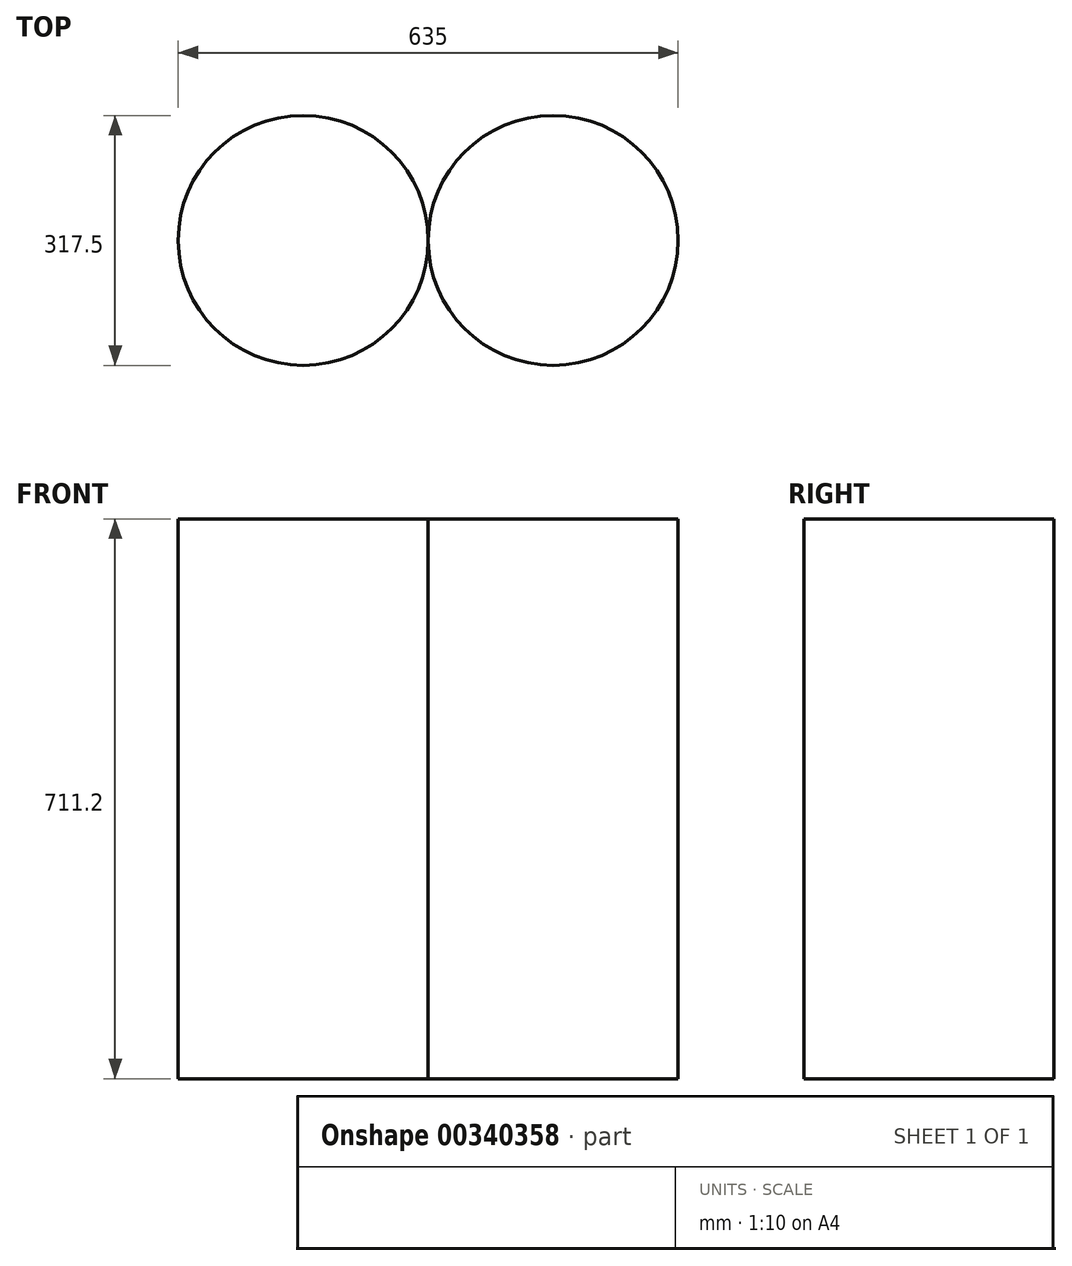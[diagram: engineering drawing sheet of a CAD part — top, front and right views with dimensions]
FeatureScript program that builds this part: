
annotation { "Feature Type Name" : "Feature", "Feature Type Description" : "" }
export const myFeature = defineFeature(function(context is Context, id is Id, definition is map)
    precondition{}
    {
        {
            var Q0;
            Q0=qCreatedBy(makeId("Top.planeOp"),FACE);
            var sketch = newSketch(context, id + "F0", { "sketchPlane" : qUnion([Q0])});
            skCircle(sketch, "E0", {"center": v(0, 0) * mm, "radius": 158.75 * mm});
            skSolve(sketch);
        }
        {
            var Q0;
            Q0=makeQuery(id+"F0.imprint","IMPRINT",FACE,{"disambiguationData":[TD([[makeQuery(id+"F0.imprint","IMPRINT",EDGE,{"derivedFrom":sQuery(id+"F0.wireOp",EDGE,"E0")}),1.0]])]});
            var sketch = newSketch(context, id + "F1", { "sketchPlane" : qUnion([Q0])});
            skLineSegment(sketch, "E1", {"start": v(167.13, 192.4) * mm, "end": v(167.13, -171.4) * mm});
            skSolve(sketch);
        }
        {
            var Q0;
            Q0=makeQuery(id+"F1.imprint","IMPRINT",FACE,{"disambiguationData":[TD([[makeQuery(id+"F1.imprint","IMPRINT",EDGE,{"derivedFrom":makeQuery(id+"F0.imprint","IMPRINT",EDGE,{"derivedFrom":sQuery(id+"F0.wireOp",EDGE,"E0")})}),1.0]])]});
            extrude(context, id + "F2", {"entities" : qUnion([Q0]), "oppositeDirection" : true, "depth" : 711.2 * mm});
        }
        {
            var Q0;
            Q0=makeQuery(id+"F2.opExtrude","SWEPT_BODY",BODY,{"disambiguationData":[OSD([sQuery(id+"F0.wireOp",EDGE,"E0")])]});
            var Q1;
            Q1=qCreatedBy(makeId("Right.planeOp"),FACE);
            mirror(context, id + "F3", {"operationType" : NewBodyOperationType.ADD, "entities" : qUnion([Q0]), "mirrorPlane" : qUnion([Q1])});
        }
        {
            var Q0;
            Q0=makeQuery(id+"F0.imprint","IMPRINT",FACE,{"disambiguationData":[TD([[makeQuery(id+"F0.imprint","IMPRINT",EDGE,{"derivedFrom":sQuery(id+"F0.wireOp",EDGE,"E0")}),1.0]])]});
            var sketch = newSketch(context, id + "F4", { "sketchPlane" : qUnion([Q0])});
            skCircle(sketch, "E2", {"center": v(317.5, 0) * mm, "radius": 158.75 * mm});
            skSolve(sketch);
        }
        {
            var Q0;
            Q0 = qSketchRegion(id + "F4", true);
            extrude(context, id + "F5", {"entities" : qUnion([Q0]), "oppositeDirection" : true, "depth" : 711.2 * mm});
        }
    });
